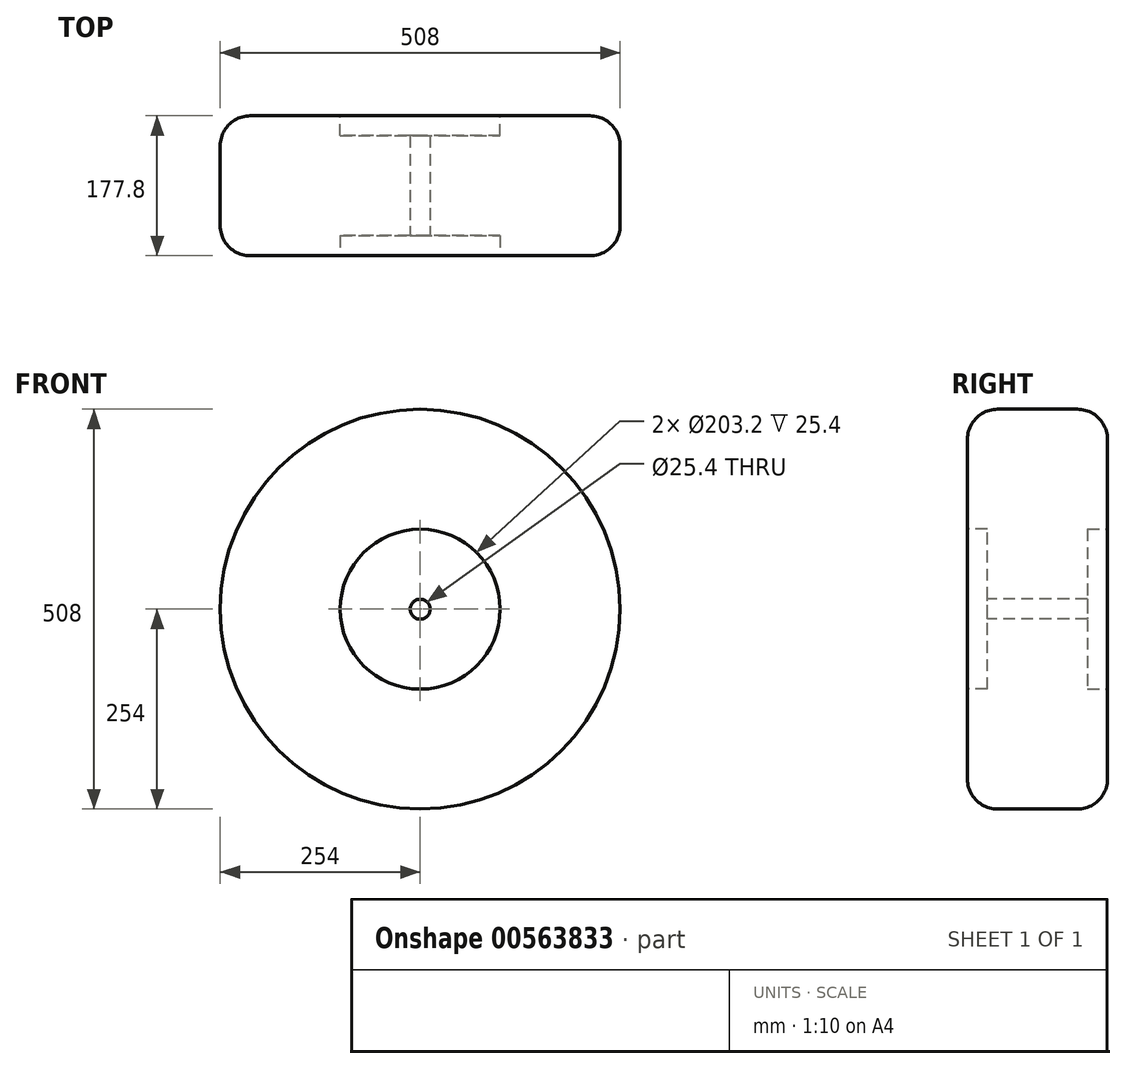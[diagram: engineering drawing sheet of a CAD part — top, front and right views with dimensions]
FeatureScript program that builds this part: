
annotation { "Feature Type Name" : "Feature", "Feature Type Description" : "" }
export const myFeature = defineFeature(function(context is Context, id is Id, definition is map)
    precondition{}
    {
        {
            var Q0;
            Q0=qCreatedBy(makeId("Front.planeOp"),FACE);
            var sketch = newSketch(context, id + "F0", { "sketchPlane" : qUnion([Q0])});
            skCircle(sketch, "E0", {"center": v(0, 0) * mm, "radius": 254 * mm});
            skSolve(sketch);
        }
        {
            var Q0;
            Q0=makeQuery(id+"F0.imprint","IMPRINT",FACE,{"disambiguationData":[TD([[makeQuery(id+"F0.imprint","IMPRINT",EDGE,{"derivedFrom":sQuery(id+"F0.wireOp",EDGE,"E0")}),1.0]])]});
            extrude(context, id + "F1", {"entities" : qUnion([Q0]), "endBound" : BoundingType.SYMMETRIC, "depth" : 177.8 * mm, "offsetDistance" : 25.4 * mm});
        }
        {
            var Q0;
            Q0=makeQuery(id+"F1.opExtrude","CAP_FACE",FACE,{"disambiguationData":[OSD([sQuery(id+"F0.wireOp",EDGE,"E0")])],"isStart":true});
            var sketch = newSketch(context, id + "F2", { "sketchPlane" : qUnion([Q0])});
            skCircle(sketch, "E1", {"center": v(0, 0) * mm, "radius": 101.6 * mm});
            skSolve(sketch);
        }
        {
            var Q0;
            Q0 = qSketchRegion(id + "F2", true);
            extrude(context, id + "F3", {"entities" : qUnion([Q0]), "operationType" : NewBodyOperationType.REMOVE, "oppositeDirection" : true, "depth" : 25.4 * mm, "offsetDistance" : 25.4 * mm});
        }
        {
            var Q0;
            Q0=makeQuery(id+"F1.opExtrude","CAP_FACE",FACE,{"disambiguationData":[OSD([sQuery(id+"F0.wireOp",EDGE,"E0")])],"isStart":false});
            var sketch = newSketch(context, id + "F4", { "sketchPlane" : qUnion([Q0])});
            skCircle(sketch, "E2", {"center": v(0, 0) * mm, "radius": 101.6 * mm});
            skSolve(sketch);
        }
        {
            var Q0;
            Q0=makeQuery(id+"F4.imprint","IMPRINT",FACE,{"disambiguationData":[TD([[makeQuery(id+"F4.imprint","IMPRINT",EDGE,{"derivedFrom":sQuery(id+"F4.wireOp",EDGE,"E2")}),1.0]])]});
            extrude(context, id + "F5", {"entities" : qUnion([Q0]), "operationType" : NewBodyOperationType.REMOVE, "oppositeDirection" : true, "depth" : 25.4 * mm, "offsetDistance" : 25.4 * mm});
        }
        {
            var Q0;
            Q0=makeQuery(id+"F1.opExtrude","CAP_EDGE",EDGE,{"disambiguationData":[OSD([sQuery(id+"F0.wireOp",EDGE,"E0")])],"isStart":true});
            var Q1;
            Q1=makeQuery(id+"F1.opExtrude","CAP_EDGE",EDGE,{"disambiguationData":[OSD([sQuery(id+"F0.wireOp",EDGE,"E0")])],"isStart":false});
            fillet(context, id + "F6", {"entities" : qUnion([Q0, Q1]), "radius" : 38.1 * mm, "tangentPropagation" : true, "allowEdgeOverflow" : false});
        }
        {
            var Q0;
            Q0=makeQuery(id+"F3.boolean.opBoolean","COPY",FACE,{"derivedFrom":makeQuery(id+"F3.opExtrude","CAP_FACE",FACE,{"disambiguationData":[OSD([sQuery(id+"F2.wireOp",EDGE,"E1")])],"isStart":false})});
            var sketch = newSketch(context, id + "F7", { "sketchPlane" : qUnion([Q0])});
            skCircle(sketch, "E3", {"center": v(0, 0) * mm, "radius": 12.7 * mm});
            skSolve(sketch);
        }
        {
            var Q0;
            Q0=makeQuery(id+"F7.imprint","IMPRINT",FACE,{"disambiguationData":[TD([[makeQuery(id+"F7.imprint","IMPRINT",EDGE,{"derivedFrom":sQuery(id+"F7.wireOp",EDGE,"E3")}),1.0]])]});
            extrude(context, id + "F8", {"entities" : qUnion([Q0]), "operationType" : NewBodyOperationType.REMOVE, "endBound" : BoundingType.SYMMETRIC, "depth" : 355.6 * mm, "offsetDistance" : 25.4 * mm});
        }
    });
